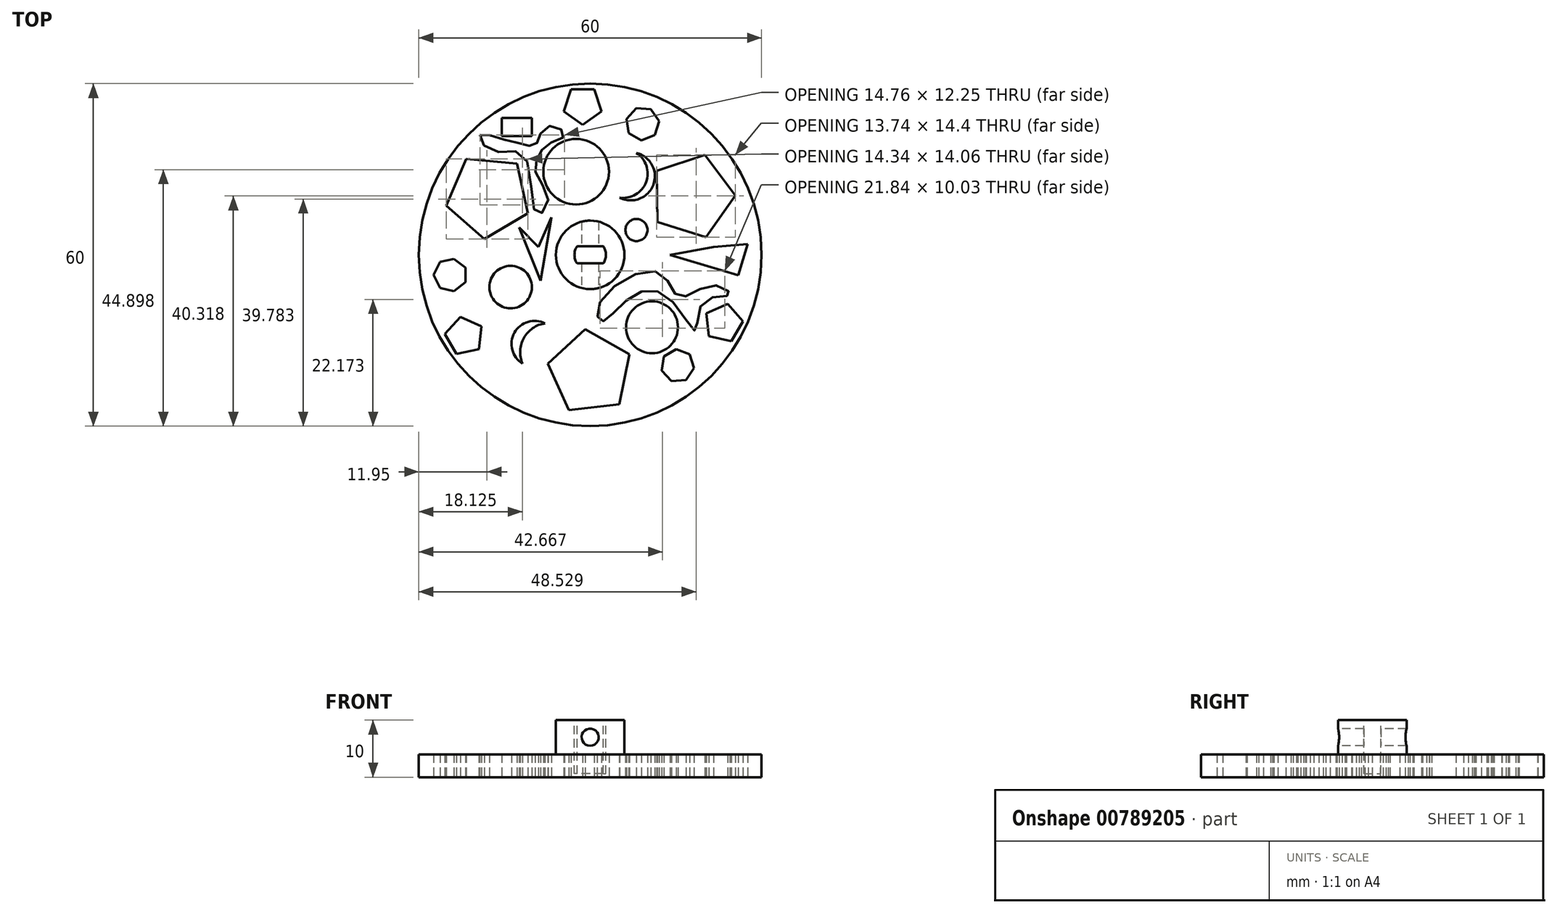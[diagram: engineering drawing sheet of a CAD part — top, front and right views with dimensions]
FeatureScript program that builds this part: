
annotation { "Feature Type Name" : "Feature", "Feature Type Description" : "" }
export const myFeature = defineFeature(function(context is Context, id is Id, definition is map)
    precondition{}
    {
        {
            var Q0;
            Q0=qCreatedBy(makeId("Top.planeOp"),FACE);
            var sketch = newSketch(context, id + "F0", { "sketchPlane" : qUnion([Q0])});
            skCircle(sketch, "E0", {"center": v(0, 0) * mm, "radius": 30 * mm});
            skCircle(sketch, "E1", {"center": v(0, 0) * mm, "radius": 6 * mm});
            skSolve(sketch);
        }
        {
            var Q0;
            Q0=makeQuery(id+"F0.imprint","IMPRINT",FACE,{"disambiguationData":[TD([[makeQuery(id+"F0.imprint","IMPRINT",EDGE,{"derivedFrom":sQuery(id+"F0.wireOp",EDGE,"E0")}),1.0]])]});
            var Q1;
            Q1=makeQuery(id+"F0.imprint","IMPRINT",FACE,{"disambiguationData":[TD([[makeQuery(id+"F0.imprint","IMPRINT",EDGE,{"derivedFrom":sQuery(id+"F0.wireOp",EDGE,"E1")}),1.0]])]});
            extrude(context, id + "F1", {"entities" : qUnion([Q0, Q1]), "oppositeDirection" : true, "depth" : 4 * mm, "offsetDistance" : 25 * mm});
        }
        {
            var Q0;
            Q0=makeQuery(id+"F0.imprint","IMPRINT",FACE,{"disambiguationData":[TD([[makeQuery(id+"F0.imprint","IMPRINT",EDGE,{"derivedFrom":sQuery(id+"F0.wireOp",EDGE,"E1")}),1.0]])]});
            extrude(context, id + "F2", {"entities" : qUnion([Q0]), "operationType" : NewBodyOperationType.ADD, "depth" : 6 * mm, "offsetDistance" : 25 * mm});
        }
        {
            var Q0;
            Q0=qCreatedBy(makeId("Front.planeOp"),FACE);
            var sketch = newSketch(context, id + "F3", { "sketchPlane" : qUnion([Q0])});
            skCircle(sketch, "E2", {"center": v(0, 3) * mm, "radius": 1.5 * mm});
            skSolve(sketch);
        }
        {
            var Q0;
            Q0=qSketchRegion(id+"F3",true);
            extrude(context, id + "F4", {"entities" : qUnion([Q0]), "operationType" : NewBodyOperationType.REMOVE, "endBound" : BoundingType.SYMMETRIC, "oppositeDirection" : true, "depth" : 25 * mm, "offsetDistance" : 25 * mm});
        }
        {
            var Q0;
            Q0=makeQuery(id+"F2.opExtrude","CAP_FACE",FACE,{"disambiguationData":[OSD([sQuery(id+"F0.wireOp",EDGE,"E1")])],"isStart":false});
            var sketch = newSketch(context, id + "F5", { "sketchPlane" : qUnion([Q0])});
            skLineSegment(sketch, "E3.bottom", {"start": v(2.3, 1.5) * mm, "end": v(-2.3, 1.5) * mm});
            skLineSegment(sketch, "E3.top", {"start": v(2.3, -1.5) * mm, "end": v(-2.3, -1.5) * mm});
            skLineSegment(sketch, "E3.left", {"start": v(2.3, 1.5) * mm, "end": v(2.3, -1.5) * mm});
            skLineSegment(sketch, "E3.right", {"start": v(-2.3, 1.5) * mm, "end": v(-2.3, -1.5) * mm});
            skPoint(sketch, "E3.middle", {"position": v(0, 0) * mm});
            skArc(sketch, "E4", {"start": v(2.3, -1.5) * mm, "mid": v(2.75, 0) * mm, "end": v(2.3, 1.5) * mm});
            skArc(sketch, "E5", {"start": v(-2.3, 1.5) * mm, "mid": v(-2.75, 0) * mm, "end": v(-2.3, -1.5) * mm});
            skSolve(sketch);
        }
        {
            var Q0;
            Q0=qSketchRegion(id+"F5",true);
            extrude(context, id + "F6", {"entities" : qUnion([Q0]), "operationType" : NewBodyOperationType.REMOVE, "oppositeDirection" : true, "depth" : 9.4 * mm, "offsetDistance" : 25 * mm});
        }
        {
            var Q0;
            Q0=qCreatedBy(makeId("Front.planeOp"),FACE);
            var sketch = newSketch(context, id + "F7", { "sketchPlane" : qUnion([Q0])});
            skLineSegment(sketch, "E6", {"start": v(0, -14.23) * mm, "end": v(0, 11.98) * mm, "construction": true});
            skLineSegment(sketch, "E7", {"start": v(30, 0) * mm, "end": v(30, -4) * mm, "construction": true});
            skLineSegment(sketch, "E8", {"start": v(30, 0) * mm, "end": v(30, -4) * mm});
            skLineSegment(sketch, "E9", {"start": v(30, -0.59) * mm, "end": v(28.59, -2) * mm});
            skLineSegment(sketch, "E10", {"start": v(28.59, -2) * mm, "end": v(30, -3.41) * mm});
            skLineSegment(sketch, "E11", {"start": v(30, -2) * mm, "end": v(26.36, -2) * mm, "construction": true});
            skSolve(sketch);
        }
        {
            var Q0;
            Q0=makeQuery(id+"F1.opExtrude","CAP_FACE",FACE,{"disambiguationData":[OSD([sQuery(id+"F0.wireOp",EDGE,"E0")])],"isStart":false});
            var sketch = newSketch(context, id + "F8", { "sketchPlane" : qUnion([Q0])});
            skPoint(sketch, "E12.0.midPoint", {"position": v(5.04, -8.26) * mm});
            skCircle(sketch, "E13.cCircle", {"center": v(0, 20.59) * mm, "radius": 6.13 * mm, "construction": true});
            skLineSegment(sketch, "E13.0", {"start": v(6.89, 17.44) * mm, "end": v(-0.87, 13.06) * mm});
            skLineSegment(sketch, "E13.1", {"start": v(-0.87, 13.06) * mm, "end": v(-7.42, 19.09) * mm});
            skLineSegment(sketch, "E13.2", {"start": v(-7.42, 19.09) * mm, "end": v(-3.72, 27.18) * mm});
            skLineSegment(sketch, "E13.3", {"start": v(-3.72, 27.18) * mm, "end": v(5.13, 26.16) * mm});
            skLineSegment(sketch, "E13.4", {"start": v(5.13, 26.16) * mm, "end": v(6.89, 17.44) * mm});
            skPoint(sketch, "E13.0.midPoint", {"position": v(3, 15.25) * mm});
            skLineSegment(sketch, "E14.1.0", {"start": v(-25.22, -8.64) * mm, "end": v(-18.54, -2.75) * mm});
            skLineSegment(sketch, "E14.1.1", {"start": v(-12.82, -15.97) * mm, "end": v(-21.68, -16.81) * mm});
            skCircle(sketch, "E14.1.2", {"center": v(-17.83, -10.3) * mm, "radius": 6.13 * mm, "construction": true});
            skPoint(sketch, "E14.1.3", {"position": v(-14.71, -5.02) * mm});
            skLineSegment(sketch, "E14.1.4", {"start": v(-18.54, -2.75) * mm, "end": v(-10.88, -7.29) * mm});
            skLineSegment(sketch, "E14.1.5", {"start": v(-21.68, -16.81) * mm, "end": v(-25.22, -8.64) * mm});
            skLineSegment(sketch, "E14.1.6", {"start": v(-10.88, -7.29) * mm, "end": v(-12.82, -15.97) * mm});
            skLineSegment(sketch, "E14.2.0", {"start": v(20.1, -17.52) * mm, "end": v(11.66, -14.68) * mm});
            skLineSegment(sketch, "E14.2.1", {"start": v(20.24, -3.12) * mm, "end": v(25.4, -10.37) * mm});
            skCircle(sketch, "E14.2.2", {"center": v(17.83, -10.3) * mm, "radius": 6.13 * mm, "construction": true});
            skPoint(sketch, "E14.2.3", {"position": v(11.7, -10.23) * mm});
            skLineSegment(sketch, "E14.2.4", {"start": v(11.66, -14.68) * mm, "end": v(11.75, -5.78) * mm});
            skLineSegment(sketch, "E14.2.5", {"start": v(25.4, -10.37) * mm, "end": v(20.1, -17.52) * mm});
            skLineSegment(sketch, "E14.2.6", {"start": v(11.75, -5.78) * mm, "end": v(20.24, -3.12) * mm});
            skCircle(sketch, "E15.cCircle", {"center": v(-22.03, 14.23) * mm, "radius": 2.79 * mm, "construction": true});
            skLineSegment(sketch, "E15.0", {"start": v(-19.04, 12.52) * mm, "end": v(-22.73, 10.86) * mm});
            skLineSegment(sketch, "E15.1", {"start": v(-22.73, 10.86) * mm, "end": v(-25.45, 13.86) * mm});
            skLineSegment(sketch, "E15.2", {"start": v(-25.45, 13.86) * mm, "end": v(-23.44, 17.38) * mm});
            skLineSegment(sketch, "E15.3", {"start": v(-23.44, 17.38) * mm, "end": v(-19.47, 16.55) * mm});
            skLineSegment(sketch, "E15.4", {"start": v(-19.47, 16.55) * mm, "end": v(-19.04, 12.52) * mm});
            skPoint(sketch, "E15.0.midPoint", {"position": v(-20.88, 11.7) * mm});
            skLineSegment(sketch, "E16.1.0", {"start": v(-4.6, -25.14) * mm, "end": v(-1.33, -22.75) * mm});
            skPoint(sketch, "E16.1.1", {"position": v(0.32, -23.93) * mm});
            skCircle(sketch, "E16.1.2", {"center": v(-1.31, -26.2) * mm, "radius": 2.79 * mm, "construction": true});
            skLineSegment(sketch, "E16.1.3", {"start": v(-3.33, -28.99) * mm, "end": v(-4.6, -25.14) * mm});
            skLineSegment(sketch, "E16.1.4", {"start": v(0.72, -28.97) * mm, "end": v(-3.33, -28.99) * mm});
            skLineSegment(sketch, "E16.1.5", {"start": v(-1.33, -22.75) * mm, "end": v(1.96, -25.11) * mm});
            skLineSegment(sketch, "E16.1.6", {"start": v(1.96, -25.11) * mm, "end": v(0.72, -28.97) * mm});
            skLineSegment(sketch, "E16.2.0", {"start": v(24.07, 8.6) * mm, "end": v(20.36, 10.22) * mm});
            skPoint(sketch, "E16.2.1", {"position": v(20.57, 12.24) * mm});
            skCircle(sketch, "E16.2.2", {"center": v(23.34, 11.96) * mm, "radius": 2.79 * mm, "construction": true});
            skLineSegment(sketch, "E16.2.3", {"start": v(26.77, 11.61) * mm, "end": v(24.07, 8.6) * mm});
            skLineSegment(sketch, "E16.2.4", {"start": v(24.73, 15.11) * mm, "end": v(26.77, 11.61) * mm});
            skLineSegment(sketch, "E16.2.5", {"start": v(20.36, 10.22) * mm, "end": v(20.77, 14.25) * mm});
            skLineSegment(sketch, "E16.2.6", {"start": v(20.77, 14.25) * mm, "end": v(24.73, 15.11) * mm});
            skCircle(sketch, "E17.cCircle", {"center": v(-24.47, 3.54) * mm, "radius": 2.63 * mm, "construction": true});
            skLineSegment(sketch, "E17.0", {"start": v(-21.85, 4.8) * mm, "end": v(-21.85, 2.27) * mm});
            skLineSegment(sketch, "E17.1", {"start": v(-21.85, 2.27) * mm, "end": v(-23.83, 0.7) * mm});
            skLineSegment(sketch, "E17.2", {"start": v(-23.83, 0.7) * mm, "end": v(-26.3, 1.26) * mm});
            skLineSegment(sketch, "E17.3", {"start": v(-26.3, 1.26) * mm, "end": v(-27.39, 3.54) * mm});
            skLineSegment(sketch, "E17.4", {"start": v(-27.39, 3.54) * mm, "end": v(-26.3, 5.81) * mm});
            skLineSegment(sketch, "E17.5", {"start": v(-26.3, 5.81) * mm, "end": v(-23.83, 6.38) * mm});
            skLineSegment(sketch, "E17.6", {"start": v(-23.83, 6.38) * mm, "end": v(-21.85, 4.8) * mm});
            skPoint(sketch, "E17.0.midPoint", {"position": v(-21.85, 3.54) * mm});
            skLineSegment(sketch, "E18.1.0", {"start": v(8.96, -20.06) * mm, "end": v(11.31, -20.98) * mm});
            skLineSegment(sketch, "E18.1.1", {"start": v(8.11, -25.68) * mm, "end": v(6.4, -23.82) * mm});
            skLineSegment(sketch, "E18.1.2", {"start": v(10.63, -25.49) * mm, "end": v(8.11, -25.68) * mm});
            skLineSegment(sketch, "E18.1.3", {"start": v(12.06, -23.4) * mm, "end": v(10.63, -25.49) * mm});
            skLineSegment(sketch, "E18.1.4", {"start": v(6.4, -23.82) * mm, "end": v(6.77, -21.32) * mm});
            skLineSegment(sketch, "E18.1.5", {"start": v(11.31, -20.98) * mm, "end": v(12.06, -23.4) * mm});
            skCircle(sketch, "E18.1.6", {"center": v(9.18, -22.96) * mm, "radius": 2.63 * mm, "construction": true});
            skPoint(sketch, "E18.1.7", {"position": v(7.86, -20.69) * mm});
            skLineSegment(sketch, "E18.1.8", {"start": v(6.77, -21.32) * mm, "end": v(8.96, -20.06) * mm});
            skLineSegment(sketch, "E18.2.0", {"start": v(12.9, 17.79) * mm, "end": v(12.51, 20.29) * mm});
            skLineSegment(sketch, "E18.2.1", {"start": v(18.18, 19.86) * mm, "end": v(17.44, 17.45) * mm});
            skLineSegment(sketch, "E18.2.2", {"start": v(16.76, 21.95) * mm, "end": v(18.18, 19.86) * mm});
            skLineSegment(sketch, "E18.2.3", {"start": v(14.23, 22.14) * mm, "end": v(16.76, 21.95) * mm});
            skLineSegment(sketch, "E18.2.4", {"start": v(17.44, 17.45) * mm, "end": v(15.08, 16.52) * mm});
            skLineSegment(sketch, "E18.2.5", {"start": v(12.51, 20.29) * mm, "end": v(14.23, 22.14) * mm});
            skCircle(sketch, "E18.2.6", {"center": v(15.3, 19.43) * mm, "radius": 2.63 * mm, "construction": true});
            skPoint(sketch, "E18.2.7", {"position": v(13.99, 17.15) * mm});
            skLineSegment(sketch, "E18.2.8", {"start": v(15.08, 16.52) * mm, "end": v(12.9, 17.79) * mm});
            skPoint(sketch, "E18.center", {"position": v(0, 0) * mm});
            skSolve(sketch);
        }
        {
            var Q0;
            Q0 = qSketchRegion(id + "F8", true);
            extrude(context, id + "F9", {"entities" : qUnion([Q0]), "operationType" : NewBodyOperationType.REMOVE, "oppositeDirection" : true, "depth" : 25 * mm, "offsetDistance" : 25 * mm});
        }
        {
            var Q0;
            Q0=makeQuery(id+"F1.opExtrude","CAP_FACE",FACE,{"disambiguationData":[OSD([sQuery(id+"F0.wireOp",EDGE,"E0")])],"isStart":false});
            var sketch = newSketch(context, id + "F10", { "sketchPlane" : qUnion([Q0])});
            skCircle(sketch, "E19", {"center": v(-13.92, 5.65) * mm, "radius": 3.72 * mm});
            skCircle(sketch, "E20", {"center": v(-2.45, -14.56) * mm, "radius": 5.75 * mm});
            skCircle(sketch, "E21", {"center": v(10.83, 12.7) * mm, "radius": 4.54 * mm});
            skCircle(sketch, "E22", {"center": v(8.1, -4.34) * mm, "radius": 1.93 * mm});
            skLineSegment(sketch, "E23.bottom", {"start": v(-10.17, -20.8) * mm, "end": v(-15.47, -20.8) * mm});
            skLineSegment(sketch, "E23.top", {"start": v(-10.17, -23.98) * mm, "end": v(-15.47, -23.98) * mm});
            skLineSegment(sketch, "E23.left", {"start": v(-10.17, -20.8) * mm, "end": v(-10.17, -23.98) * mm});
            skLineSegment(sketch, "E23.right", {"start": v(-15.47, -20.8) * mm, "end": v(-15.47, -23.98) * mm});
            skPoint(sketch, "E23.middle", {"position": v(-12.82, -22.4) * mm});
            skPoint(sketch, "E24.middle", {"position": v(14, 0) * mm});
            skArc(sketch, "E25", {"start": v(-11.85, 19.05) * mm, "mid": v(-13.25, 13.64) * mm, "end": v(-7.9, 12) * mm});
            skPoint(sketch, "E25.startSnap0", {"position": v(-11.85, -11.63) * mm});
            skArc(sketch, "E26", {"start": v(-11.85, 19.05) * mm, "mid": v(-11.61, 14.56) * mm, "end": v(-7.9, 12) * mm});
            skArc(sketch, "E27", {"start": v(8.1, -17.85) * mm, "mid": v(11.06, -12.27) * mm, "end": v(5.15, -10.02) * mm});
            skArc(sketch, "E28", {"start": v(8.1, -17.85) * mm, "mid": v(9.8, -12.74) * mm, "end": v(5.15, -10.02) * mm});
            skLineSegment(sketch, "E29", {"start": v(14, 0) * mm, "end": v(25.93, 3.6) * mm});
            skLineSegment(sketch, "E30", {"start": v(25.93, 3.6) * mm, "end": v(27.6, -1.88) * mm});
            skLineSegment(sketch, "E31", {"start": v(27.6, -1.88) * mm, "end": v(21.62, -1.39) * mm});
            skLineSegment(sketch, "E32", {"start": v(21.62, -1.39) * mm, "end": v(14, 0) * mm});
            skLineSegment(sketch, "E33", {"start": v(-12.44, -4.8) * mm, "end": v(-8.7, 4.52) * mm});
            skLineSegment(sketch, "E34", {"start": v(-8.7, 4.52) * mm, "end": v(-6.77, -6.61) * mm});
            skLineSegment(sketch, "E35", {"start": v(-6.77, -6.61) * mm, "end": v(-9.04, -1.39) * mm});
            skLineSegment(sketch, "E36", {"start": v(-9.04, -1.39) * mm, "end": v(-12.44, -4.8) * mm});
            skFitSpline(sketch, "E37", {"points": [v(1.75, 8.26) * mm, v(11.97, 3.04) * mm, v(15.6, 7.35) * mm, v(21.62, 5.31) * mm, v(24.45, 7.01) * mm, v(19.91, 8.15) * mm, v(18.44, 13.26) * mm, v(13.1, 7.01) * mm, v(6.29, 8.04) * mm, v(1.97, 11.67) * mm, v(1.75, 8.26) * mm]});
            skPoint(sketch, "E38.1.internal.snap0", {"position": v(-17.25, -16.4) * mm});
            skPoint(sketch, "E38.13.internal.snap0", {"position": v(10.14, -20.52) * mm});
            skFitSpline(sketch, "E38", {"points": [v(-19.26, -20.98) * mm, v(-17.25, -18.2) * mm, v(-11.54, -17.4) * mm, v(-9.38, -7.18) * mm, v(-7.34, -9.34) * mm, v(-9.5, -14.25) * mm, v(-9.04, -17.4) * mm, v(-7.1, -19.55) * mm, v(-4.5, -20.98) * mm, v(-6.54, -22.62) * mm, v(-8.81, -20.98) * mm, v(-9.6, -19.21) * mm, v(-12.44, -19.55) * mm, v(-16.2, -20.52) * mm, v(-19.26, -20.98) * mm]});
            skSolve(sketch);
        }
        {
            var Q0;
            Q0 = qSketchRegion(id + "F10", true);
            extrude(context, id + "F11", {"entities" : qUnion([Q0]), "operationType" : NewBodyOperationType.REMOVE, "oppositeDirection" : true, "depth" : 25 * mm, "offsetDistance" : 25 * mm});
        }
    });
